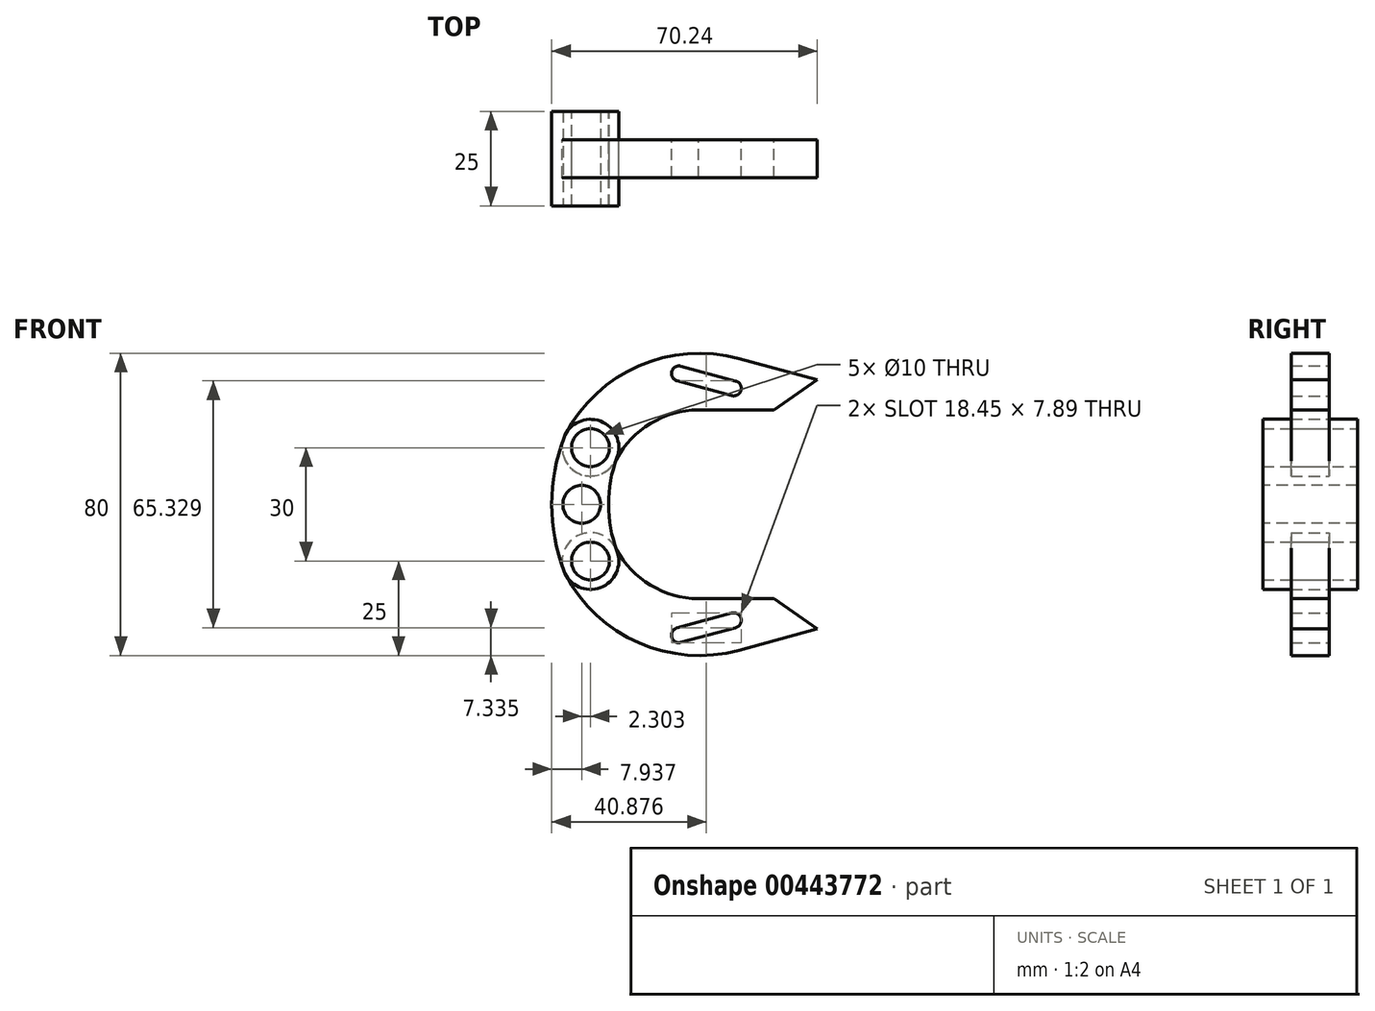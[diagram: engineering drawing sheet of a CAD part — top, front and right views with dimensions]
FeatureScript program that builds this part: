
annotation { "Feature Type Name" : "Feature", "Feature Type Description" : "" }
export const myFeature = defineFeature(function(context is Context, id is Id, definition is map)
    precondition{}
    {
        {
            var Q0;
            Q0=qCreatedBy(makeId("Front.planeOp"),FACE);
            var sketch = newSketch(context, id + "F0", { "sketchPlane" : qUnion([Q0])});
            skLineSegment(sketch, "E0", {"start": v(0, 15) * mm, "end": v(0, -15) * mm, "construction": true});
            skLineSegment(sketch, "E1", {"start": v(0, 0) * mm, "end": v(80, 0) * mm, "construction": true});
            skCircle(sketch, "E2", {"center": v(0, 15) * mm, "radius": 5 * mm});
            skCircle(sketch, "E3", {"center": v(0, -15) * mm, "radius": 5 * mm});
            skArc(sketch, "E4.0", {"start": v(7.02, 12.35) * mm, "mid": v(2.65, 22.02) * mm, "end": v(-7.02, 17.65) * mm});
            skArc(sketch, "E5.0", {"start": v(-7.02, -17.65) * mm, "mid": v(2.65, -22.02) * mm, "end": v(7.02, -12.35) * mm});
            skArc(sketch, "E6", {"start": v(-7.02, 17.65) * mm, "mid": v(-10.24, 0) * mm, "end": v(-7.02, -17.65) * mm});
            skArc(sketch, "E7", {"start": v(7.02, 12.35) * mm, "mid": v(4.76, 0) * mm, "end": v(7.02, -12.35) * mm});
            skSolve(sketch);
        }
        {
            var Q0;
            Q0 = qSketchRegion(id + "F0", true);
            extrude(context, id + "F1", {"entities" : qUnion([Q0]), "endBound" : BoundingType.SYMMETRIC, "depth" : 25 * mm});
        }
        {
            var Q0;
            Q0=qCreatedBy(makeId("Front.planeOp"),FACE);
            var sketch = newSketch(context, id + "F2", { "sketchPlane" : qUnion([Q0])});
            skCircle(sketch, "E8.0", {"center": v(0, 15) * mm, "radius": 5 * mm});
            skCircle(sketch, "E9", {"center": v(0, 15) * mm, "radius": 7.5 * mm});
            skCircle(sketch, "E10.MirrorC", {"center": v(0, -15) * mm, "radius": 7.5 * mm});
            skCircle(sketch, "E11.MirrorC", {"center": v(0, -15) * mm, "radius": 5 * mm});
            skLineSegment(sketch, "E12", {"start": v(0, 0) * mm, "end": v(45.46, 0) * mm, "construction": true});
            skArc(sketch, "E13", {"start": v(28.5, 25) * mm, "mid": v(15.72, 21.29) * mm, "end": v(6.65, 11.54) * mm});
            skArc(sketch, "E14", {"start": v(39.3, 38.6) * mm, "mid": v(12.77, 36.63) * mm, "end": v(-6.65, 18.46) * mm});
            skLineSegment(sketch, "E15", {"start": v(39.3, 38.6) * mm, "end": v(60, 33) * mm});
            skLineSegment(sketch, "E16", {"start": v(60, 33) * mm, "end": v(48.5, 25) * mm});
            skLineSegment(sketch, "E17", {"start": v(48.5, 25) * mm, "end": v(28.5, 25) * mm});
            skLineSegment(sketch, "E18", {"start": v(23.4, 34.63) * mm, "end": v(37.87, 30.7) * mm, "construction": true});
            skLineSegment(sketch, "E19", {"start": v(37.87, 30.7) * mm, "end": v(39.3, 38.6) * mm, "construction": true});
            skArc(sketch, "E20", {"start": v(23.92, 36.56) * mm, "mid": v(21.47, 35.15) * mm, "end": v(22.87, 32.7) * mm});
            skArc(sketch, "E21", {"start": v(37.35, 28.77) * mm, "mid": v(39.83, 30.27) * mm, "end": v(38.23, 32.67) * mm});
            skLineSegment(sketch, "E22", {"start": v(23.92, 36.56) * mm, "end": v(38.4, 32.63) * mm});
            skLineSegment(sketch, "E23", {"start": v(22.87, 32.7) * mm, "end": v(37.35, 28.77) * mm});
            skArc(sketch, "E24.MirrorCS", {"start": v(37.35, -28.77) * mm, "mid": v(39.83, -30.27) * mm, "end": v(38.23, -32.67) * mm});
            skArc(sketch, "E25.MirrorCS", {"start": v(23.92, -36.56) * mm, "mid": v(21.47, -35.15) * mm, "end": v(22.87, -32.7) * mm});
            skLineSegment(sketch, "E26.MirrorCS", {"start": v(39.3, -38.6) * mm, "end": v(60, -33) * mm});
            skArc(sketch, "E27.MirrorCS", {"start": v(28.5, -25) * mm, "mid": v(15.72, -21.29) * mm, "end": v(6.65, -11.54) * mm});
            skLineSegment(sketch, "E28.MirrorCS", {"start": v(23.4, -34.63) * mm, "end": v(37.87, -30.7) * mm, "construction": true});
            skLineSegment(sketch, "E29.MirrorCS", {"start": v(37.87, -30.7) * mm, "end": v(39.3, -38.6) * mm, "construction": true});
            skLineSegment(sketch, "E30.MirrorCS", {"start": v(23.92, -36.56) * mm, "end": v(38.4, -32.63) * mm});
            skLineSegment(sketch, "E31.MirrorCS", {"start": v(60, -33) * mm, "end": v(48.5, -25) * mm});
            skLineSegment(sketch, "E32.MirrorCS", {"start": v(22.87, -32.7) * mm, "end": v(37.35, -28.77) * mm});
            skArc(sketch, "E33.MirrorCS", {"start": v(39.3, -38.6) * mm, "mid": v(12.77, -36.63) * mm, "end": v(-6.65, -18.46) * mm});
            skLineSegment(sketch, "E34.MirrorCS", {"start": v(48.5, -25) * mm, "end": v(28.5, -25) * mm});
            skSolve(sketch);
        }
        {
            var Q0;
            Q0 = qSketchRegion(id + "F2", true);
            extrude(context, id + "F3", {"entities" : qUnion([Q0]), "endBound" : BoundingType.SYMMETRIC, "depth" : 10 * mm});
        }
        {
            var Q0;
            Q0=makeQuery(id+"F1.opExtrude","CAP_FACE",FACE,{"disambiguationData":[OSD([sQuery(id+"F0.wireOp",EDGE,"E2"),sQuery(id+"F0.wireOp",EDGE,"E3"),sQuery(id+"F0.wireOp",EDGE,"E4.0"),sQuery(id+"F0.wireOp",EDGE,"E5.0"),sQuery(id+"F0.wireOp",EDGE,"E6"),sQuery(id+"F0.wireOp",EDGE,"E7")])],"isStart":false});
            var sketch = newSketch(context, id + "F4", { "sketchPlane" : qUnion([Q0])});
            skArc(sketch, "E35", {"start": v(0, 15) * mm, "mid": v(-2.3, 0) * mm, "end": v(0, -15) * mm, "construction": true});
            skCircle(sketch, "E36", {"center": v(-2.3, 0) * mm, "radius": 5 * mm});
            skSolve(sketch);
        }
        {
            var Q0;
            Q0 = qSketchRegion(id + "F4", true);
            extrude(context, id + "F5", {"entities" : qUnion([Q0]), "operationType" : NewBodyOperationType.REMOVE, "endBound" : BoundingType.THROUGH_ALL, "oppositeDirection" : true, "depth" : 25 * mm});
        }
    });
